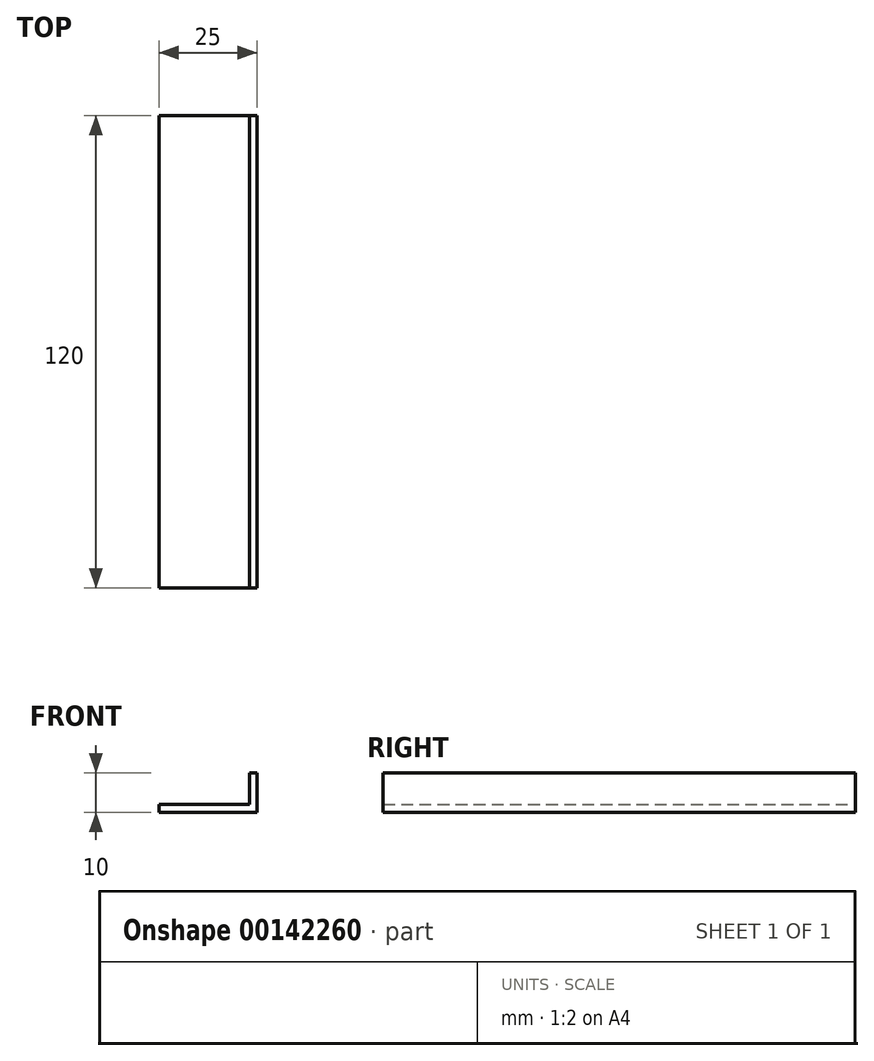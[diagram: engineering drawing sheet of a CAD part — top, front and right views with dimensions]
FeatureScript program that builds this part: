
annotation { "Feature Type Name" : "Feature", "Feature Type Description" : "" }
export const myFeature = defineFeature(function(context is Context, id is Id, definition is map)
    precondition{}
    {
        {
            var Q0;
            Q0=qCreatedBy(makeId("Front.planeOp"),FACE);
            var sketch = newSketch(context, id + "F0", { "sketchPlane" : qUnion([Q0])});
            skLineSegment(sketch, "E0", {"start": v(0, 0) * mm, "end": v(25, 0) * mm});
            skLineSegment(sketch, "E1", {"start": v(25, 0) * mm, "end": v(25, 10) * mm});
            skLineSegment(sketch, "E2", {"start": v(25, 10) * mm, "end": v(23, 10) * mm});
            skLineSegment(sketch, "E3", {"start": v(23, 10) * mm, "end": v(23, 2) * mm});
            skLineSegment(sketch, "E4", {"start": v(23, 2) * mm, "end": v(0, 2) * mm});
            skLineSegment(sketch, "E5", {"start": v(0, 2) * mm, "end": v(0, 0) * mm});
            skSolve(sketch);
        }
        {
            var Q0;
            Q0 = qSketchRegion(id + "F0", true);
            extrude(context, id + "F1", {"entities" : qUnion([Q0]), "depth" : 120 * mm});
        }
    });
